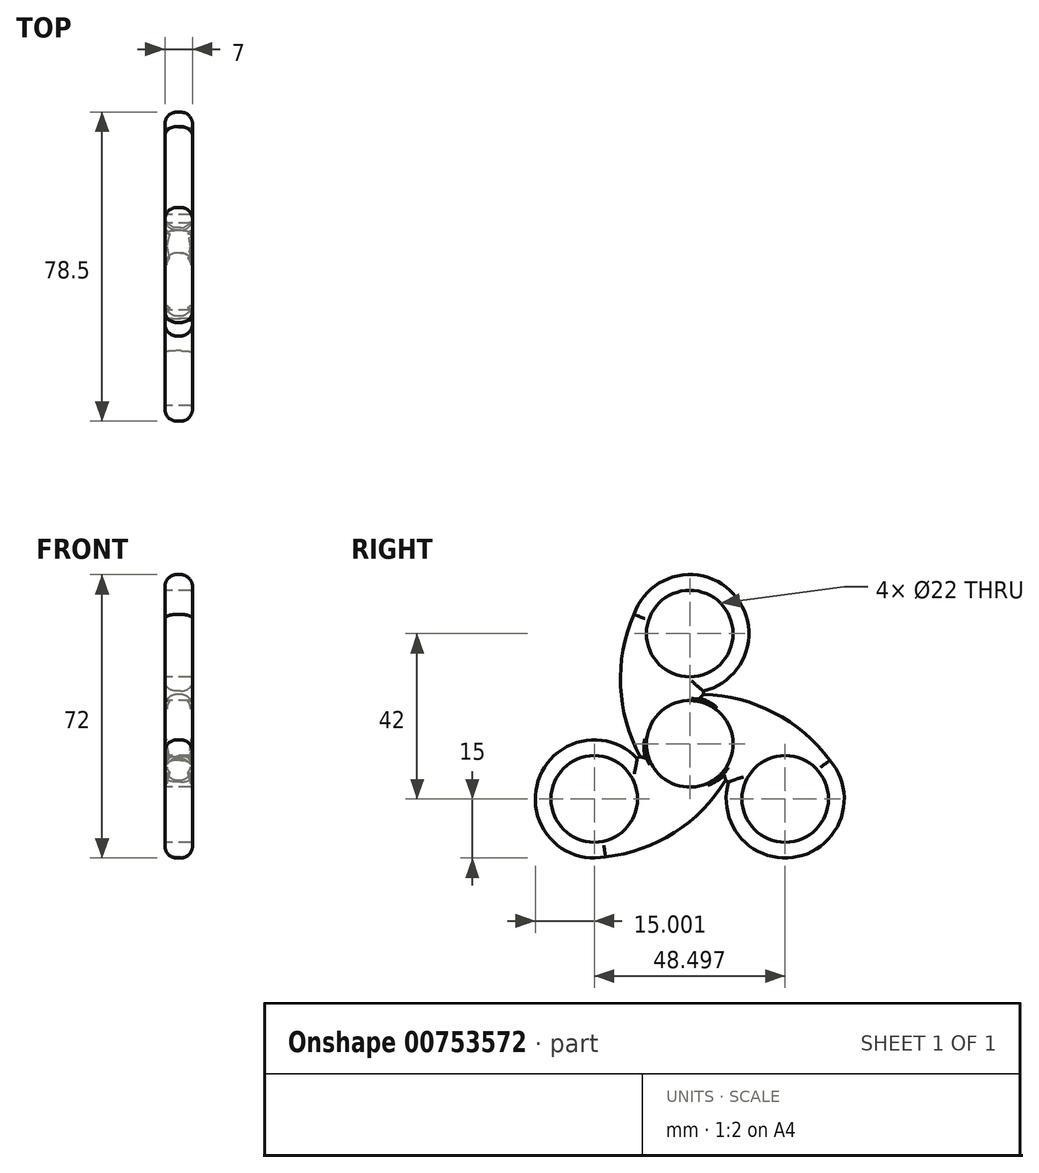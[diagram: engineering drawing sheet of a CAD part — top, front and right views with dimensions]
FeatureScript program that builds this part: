
annotation { "Feature Type Name" : "Feature", "Feature Type Description" : "" }
export const myFeature = defineFeature(function(context is Context, id is Id, definition is map)
    precondition{}
    {
        {
            var Q0;
            Q0=qCreatedBy(makeId("Right.planeOp"),FACE);
            var sketch = newSketch(context, id + "F0", { "sketchPlane" : qUnion([Q0])});
            skCircle(sketch, "E0", {"center": v(0, 0) * mm, "radius": 13 * mm});
            skCircle(sketch, "E1", {"center": v(0, 0) * mm, "radius": 11 * mm});
            skPoint(sketch, "E2", {"position": v(0, 28) * mm});
            skCircle(sketch, "E3", {"center": v(0, 28) * mm, "radius": 15 * mm});
            skCircle(sketch, "E4", {"center": v(0, 28) * mm, "radius": 11 * mm});
            skCircle(sketch, "E5.1.0", {"center": v(-24.25, -14) * mm, "radius": 15 * mm});
            skCircle(sketch, "E5.2.0", {"center": v(24.25, -14) * mm, "radius": 15 * mm});
            skCircle(sketch, "E6.1.0", {"center": v(-24.25, -14) * mm, "radius": 11 * mm});
            skCircle(sketch, "E6.2.0", {"center": v(24.25, -14) * mm, "radius": 11 * mm});
            skArc(sketch, "E7", {"start": v(-12.54, 36.23) * mm, "mid": v(-17.6, 16.5) * mm, "end": v(-12.58, -3.26) * mm});
            skArc(sketch, "E8.1.1", {"start": v(-25.1, -28.98) * mm, "mid": v(-5.48, -23.5) * mm, "end": v(9.12, -9.27) * mm});
            skArc(sketch, "E8.2.1", {"start": v(37.65, -7.26) * mm, "mid": v(23.09, 7) * mm, "end": v(3.47, 12.53) * mm});
            skArc(sketch, "E9", {"start": v(-12, 19) * mm, "mid": v(-12.12, 13.22) * mm, "end": v(-10.51, 7.65) * mm});
            skArc(sketch, "E10.1.0", {"start": v(-10.46, -19.9) * mm, "mid": v(-5.38, -17.1) * mm, "end": v(-1.37, -12.93) * mm});
            skArc(sketch, "E10.2.0", {"start": v(22.47, 0.9) * mm, "mid": v(17.5, 3.9) * mm, "end": v(11.88, 5.28) * mm});
            skLineSegment(sketch, "E11", {"start": v(-12.58, -3.26) * mm, "end": v(-13.35, -3.7) * mm});
            skLineSegment(sketch, "E12.1.0", {"start": v(9.12, -9.27) * mm, "end": v(9.88, -9.7) * mm});
            skLineSegment(sketch, "E12.2.0", {"start": v(3.47, 12.53) * mm, "end": v(3.47, 13.4) * mm});
            skLineSegment(sketch, "E13", {"start": v(-4.37, 12.24) * mm, "end": v(-4.37, 13.65) * mm});
            skLineSegment(sketch, "E14.1.0", {"start": v(-8.42, -9.9) * mm, "end": v(-9.64, -10.61) * mm});
            skLineSegment(sketch, "E14.2.0", {"start": v(12.79, -2.34) * mm, "end": v(14, -3.04) * mm});
            skSolve(sketch);
        }
        {
            var Q0;
            Q0 = qSketchRegion(id + "F0", true);
            var Q1;
            {var subQ0=sQuery(id+"F0.wireOp",EDGE,"E13");Q1=makeQuery(id+"F0.imprint","IMPRINT",FACE,{"disambiguationData":[TD([[makeQuery(id+"F0.imprint","IMPRINT",EDGE,{"derivedFrom":subQ0}),-1.0]])]});}
            var Q2;
            {var subQ0=sQuery(id+"F0.wireOp",EDGE,"E14.2.0");Q2=makeQuery(id+"F0.imprint","IMPRINT",FACE,{"disambiguationData":[TD([[makeQuery(id+"F0.imprint","IMPRINT",EDGE,{"derivedFrom":subQ0}),-1.0]])]});}
            var Q3;
            {var subQ0=sQuery(id+"F0.wireOp",EDGE,"E14.1.0");Q3=makeQuery(id+"F0.imprint","IMPRINT",FACE,{"disambiguationData":[TD([[makeQuery(id+"F0.imprint","IMPRINT",EDGE,{"derivedFrom":subQ0}),-1.0]])]});}
            var Q4;
            {var subQ0=sQuery(id+"F0.wireOp",EDGE,"E9");Q4=makeQuery(id+"F0.imprint","IMPRINT",FACE,{"disambiguationData":[TD([[makeQuery(id+"F0.imprint","IMPRINT",EDGE,{"derivedFrom":subQ0}),1.0]])]});}
            var Q5;
            {var subQ0=sQuery(id+"F0.wireOp",EDGE,"E10.2.0");Q5=makeQuery(id+"F0.imprint","IMPRINT",FACE,{"disambiguationData":[TD([[makeQuery(id+"F0.imprint","IMPRINT",EDGE,{"derivedFrom":subQ0}),1.0]])]});}
            var Q6;
            {var subQ0=sQuery(id+"F0.wireOp",EDGE,"E10.1.0");Q6=makeQuery(id+"F0.imprint","IMPRINT",FACE,{"disambiguationData":[TD([[makeQuery(id+"F0.imprint","IMPRINT",EDGE,{"derivedFrom":subQ0}),1.0]])]});}
            extrude(context, id + "F1", {"entities" : qUnion([Q0, Q1, Q2, Q3, Q4, Q5, Q6]), "depth" : 7 * mm, "offsetDistance" : 25.4 * mm});
        }
        {
            var Q0;
            {var subQ0=sQuery(id+"F0.wireOp",EDGE,"E0");Q0=makeQuery(id+"F1.opExtrude","CAP_EDGE",EDGE,{"disambiguationData":[OSD([subQ0]),TDD([makeQuery(id+"F0.imprint","IMPRINT",EDGE,{"disambiguationData":[TD([[makeQuery(id+"F0.imprint","INTERSECT",VERTEX,{"derivedFrom":[subQ0,sQuery(id+"F0.wireOp",EDGE,"E10.1.0")]}),1.0]])],"derivedFrom":subQ0})])],"isStart":true});}
            var Q1;
            Q1=makeQuery(id+"F1.opExtrude","CAP_EDGE",EDGE,{"disambiguationData":[OSD([sQuery(id+"F0.wireOp",EDGE,"E14.1.0")])],"isStart":true});
            var Q2;
            {var subQ0=sQuery(id+"F0.wireOp",EDGE,"E5.1.0");Q2=makeQuery(id+"F1.opExtrude","CAP_EDGE",EDGE,{"disambiguationData":[OSD([subQ0]),TDD([makeQuery(id+"F0.imprint","IMPRINT",EDGE,{"disambiguationData":[TD([[makeQuery(id+"F0.imprint","INTERSECT",VERTEX,{"derivedFrom":[subQ0,sQuery(id+"F0.wireOp",EDGE,"E10.1.0")]}),-1.0]])],"derivedFrom":subQ0})])],"isStart":true});}
            var Q3;
            Q3=makeQuery(id+"F1.opExtrude","CAP_EDGE",EDGE,{"disambiguationData":[OSD([sQuery(id+"F0.wireOp",EDGE,"E10.1.0")])],"isStart":true});
            var Q4;
            Q4=makeQuery(id+"F1.opExtrude","CAP_EDGE",EDGE,{"disambiguationData":[OSD([sQuery(id+"F0.wireOp",EDGE,"E10.2.0")])],"isStart":true});
            var Q5;
            {var subQ0=sQuery(id+"F0.wireOp",EDGE,"E5.2.0");Q5=makeQuery(id+"F1.opExtrude","CAP_EDGE",EDGE,{"disambiguationData":[OSD([subQ0]),TDD([makeQuery(id+"F0.imprint","IMPRINT",EDGE,{"disambiguationData":[TD([[makeQuery(id+"F0.imprint","INTERSECT",VERTEX,{"derivedFrom":[subQ0,sQuery(id+"F0.wireOp",EDGE,"E10.2.0")]}),-1.0]])],"derivedFrom":subQ0})])],"isStart":true});}
            var Q6;
            Q6=makeQuery(id+"F1.opExtrude","CAP_EDGE",EDGE,{"disambiguationData":[OSD([sQuery(id+"F0.wireOp",EDGE,"E14.2.0")])],"isStart":true});
            var Q7;
            {var subQ0=sQuery(id+"F0.wireOp",EDGE,"E0");Q7=makeQuery(id+"F1.opExtrude","CAP_EDGE",EDGE,{"disambiguationData":[OSD([subQ0]),TDD([makeQuery(id+"F0.imprint","IMPRINT",EDGE,{"disambiguationData":[TD([[makeQuery(id+"F0.imprint","INTERSECT",VERTEX,{"derivedFrom":[subQ0,sQuery(id+"F0.wireOp",EDGE,"E10.2.0")]}),1.0]])],"derivedFrom":subQ0})])],"isStart":true});}
            var Q8;
            Q8=makeQuery(id+"F1.opExtrude","CAP_EDGE",EDGE,{"disambiguationData":[OSD([sQuery(id+"F0.wireOp",EDGE,"E13")])],"isStart":true});
            var Q9;
            {var subQ0=sQuery(id+"F0.wireOp",EDGE,"E0");Q9=makeQuery(id+"F1.opExtrude","CAP_EDGE",EDGE,{"disambiguationData":[OSD([subQ0]),TDD([makeQuery(id+"F0.imprint","IMPRINT",EDGE,{"disambiguationData":[TD([[makeQuery(id+"F0.imprint","INTERSECT",VERTEX,{"derivedFrom":[subQ0,sQuery(id+"F0.wireOp",EDGE,"E9")]}),1.0]])],"derivedFrom":subQ0})])],"isStart":true});}
            var Q10;
            Q10=makeQuery(id+"F1.opExtrude","CAP_EDGE",EDGE,{"disambiguationData":[OSD([sQuery(id+"F0.wireOp",EDGE,"E9")])],"isStart":true});
            var Q11;
            {var subQ0=sQuery(id+"F0.wireOp",EDGE,"E3");Q11=makeQuery(id+"F1.opExtrude","CAP_EDGE",EDGE,{"disambiguationData":[OSD([subQ0]),TDD([makeQuery(id+"F0.imprint","IMPRINT",EDGE,{"disambiguationData":[TD([[makeQuery(id+"F0.imprint","INTERSECT",VERTEX,{"derivedFrom":[subQ0,sQuery(id+"F0.wireOp",EDGE,"E9")]}),-1.0]])],"derivedFrom":subQ0})])],"isStart":true});}
            var Q12;
            {var subQ0=sQuery(id+"F0.wireOp",EDGE,"E0");Q12=makeQuery(id+"F1.opExtrude","CAP_EDGE",EDGE,{"disambiguationData":[OSD([subQ0]),TDD([makeQuery(id+"F0.imprint","IMPRINT",EDGE,{"disambiguationData":[TD([[makeQuery(id+"F0.imprint","INTERSECT",VERTEX,{"derivedFrom":[subQ0,sQuery(id+"F0.wireOp",EDGE,"E9")]}),1.0]])],"derivedFrom":subQ0})])],"isStart":false});}
            var Q13;
            Q13=makeQuery(id+"F1.opExtrude","CAP_EDGE",EDGE,{"disambiguationData":[OSD([sQuery(id+"F0.wireOp",EDGE,"E9")])],"isStart":false});
            var Q14;
            Q14=makeQuery(id+"F1.opExtrude","CAP_EDGE",EDGE,{"disambiguationData":[OSD([sQuery(id+"F0.wireOp",EDGE,"E13")])],"isStart":false});
            var Q15;
            {var subQ0=sQuery(id+"F0.wireOp",EDGE,"E3");Q15=makeQuery(id+"F1.opExtrude","CAP_EDGE",EDGE,{"disambiguationData":[OSD([subQ0]),TDD([makeQuery(id+"F0.imprint","IMPRINT",EDGE,{"disambiguationData":[TD([[makeQuery(id+"F0.imprint","INTERSECT",VERTEX,{"derivedFrom":[subQ0,sQuery(id+"F0.wireOp",EDGE,"E9")]}),-1.0]])],"derivedFrom":subQ0})])],"isStart":false});}
            var Q16;
            {var subQ0=sQuery(id+"F0.wireOp",EDGE,"E0");Q16=makeQuery(id+"F1.opExtrude","CAP_EDGE",EDGE,{"disambiguationData":[OSD([subQ0]),TDD([makeQuery(id+"F0.imprint","IMPRINT",EDGE,{"disambiguationData":[TD([[makeQuery(id+"F0.imprint","INTERSECT",VERTEX,{"derivedFrom":[subQ0,sQuery(id+"F0.wireOp",EDGE,"E10.2.0")]}),1.0]])],"derivedFrom":subQ0})])],"isStart":false});}
            var Q17;
            Q17=makeQuery(id+"F1.opExtrude","CAP_EDGE",EDGE,{"disambiguationData":[OSD([sQuery(id+"F0.wireOp",EDGE,"E10.2.0")])],"isStart":false});
            var Q18;
            {var subQ0=sQuery(id+"F0.wireOp",EDGE,"E5.2.0");Q18=makeQuery(id+"F1.opExtrude","CAP_EDGE",EDGE,{"disambiguationData":[OSD([subQ0]),TDD([makeQuery(id+"F0.imprint","IMPRINT",EDGE,{"disambiguationData":[TD([[makeQuery(id+"F0.imprint","INTERSECT",VERTEX,{"derivedFrom":[subQ0,sQuery(id+"F0.wireOp",EDGE,"E10.2.0")]}),-1.0]])],"derivedFrom":subQ0})])],"isStart":false});}
            var Q19;
            Q19=makeQuery(id+"F1.opExtrude","CAP_EDGE",EDGE,{"disambiguationData":[OSD([sQuery(id+"F0.wireOp",EDGE,"E14.2.0")])],"isStart":false});
            var Q20;
            {var subQ0=sQuery(id+"F0.wireOp",EDGE,"E7");var subQ1=sQuery(id+"F0.wireOp",EDGE,"E3");var subQ2=makeQuery(id+"F0.imprint","INTERSECT",VERTEX,{"disambiguationData":[OD(0.0)],"derivedFrom":[subQ1,subQ0]});Q20=makeQuery(id+"F1.opExtrude","CAP_EDGE",EDGE,{"disambiguationData":[OSD([subQ1]),TDD([makeQuery(id+"F0.imprint","IMPRINT",EDGE,{"disambiguationData":[TD([[subQ2,-1.0]])],"derivedFrom":subQ1}),makeQuery(id+"F0.imprint","IMPRINT",EDGE,{"disambiguationData":[TD([[subQ2,1.0]])],"derivedFrom":subQ1})])],"isStart":true});}
            var Q21;
            {var subQ0=sQuery(id+"F0.wireOp",EDGE,"E7");var subQ1=sQuery(id+"F0.wireOp",EDGE,"E3");var subQ2=makeQuery(id+"F0.imprint","INTERSECT",VERTEX,{"disambiguationData":[OD(0.0)],"derivedFrom":[subQ1,subQ0]});Q21=makeQuery(id+"F1.opExtrude","CAP_EDGE",EDGE,{"disambiguationData":[OSD([subQ1]),TDD([makeQuery(id+"F0.imprint","IMPRINT",EDGE,{"disambiguationData":[TD([[subQ2,-1.0]])],"derivedFrom":subQ1}),makeQuery(id+"F0.imprint","IMPRINT",EDGE,{"disambiguationData":[TD([[subQ2,1.0]])],"derivedFrom":subQ1})])],"isStart":false});}
            var Q22;
            Q22=makeQuery(id+"F1.opExtrude","CAP_EDGE",EDGE,{"disambiguationData":[OSD([sQuery(id+"F0.wireOp",EDGE,"E8.2.1")])],"isStart":false});
            var Q23;
            Q23=makeQuery(id+"F1.opExtrude","CAP_EDGE",EDGE,{"disambiguationData":[OSD([sQuery(id+"F0.wireOp",EDGE,"E8.2.1")])],"isStart":true});
            var Q24;
            Q24=makeQuery(id+"F1.opExtrude","CAP_EDGE",EDGE,{"disambiguationData":[OSD([sQuery(id+"F0.wireOp",EDGE,"E8.1.1")])],"isStart":true});
            var Q25;
            Q25=makeQuery(id+"F1.opExtrude","CAP_EDGE",EDGE,{"disambiguationData":[OSD([sQuery(id+"F0.wireOp",EDGE,"E8.1.1")])],"isStart":false});
            var Q26;
            {var subQ0=sQuery(id+"F0.wireOp",EDGE,"E8.1.1");var subQ1=sQuery(id+"F0.wireOp",EDGE,"E5.1.0");var subQ2=makeQuery(id+"F0.imprint","INTERSECT",VERTEX,{"disambiguationData":[OD(0.0)],"derivedFrom":[subQ1,subQ0]});Q26=makeQuery(id+"F1.opExtrude","CAP_EDGE",EDGE,{"disambiguationData":[OSD([subQ1]),TDD([makeQuery(id+"F0.imprint","IMPRINT",EDGE,{"disambiguationData":[TD([[subQ2,-1.0]])],"derivedFrom":subQ1}),makeQuery(id+"F0.imprint","IMPRINT",EDGE,{"disambiguationData":[TD([[subQ2,1.0]])],"derivedFrom":subQ1})])],"isStart":true});}
            var Q27;
            {var subQ0=sQuery(id+"F0.wireOp",EDGE,"E8.1.1");var subQ1=sQuery(id+"F0.wireOp",EDGE,"E5.1.0");var subQ2=makeQuery(id+"F0.imprint","INTERSECT",VERTEX,{"disambiguationData":[OD(0.0)],"derivedFrom":[subQ1,subQ0]});Q27=makeQuery(id+"F1.opExtrude","CAP_EDGE",EDGE,{"disambiguationData":[OSD([subQ1]),TDD([makeQuery(id+"F0.imprint","IMPRINT",EDGE,{"disambiguationData":[TD([[subQ2,-1.0]])],"derivedFrom":subQ1}),makeQuery(id+"F0.imprint","IMPRINT",EDGE,{"disambiguationData":[TD([[subQ2,1.0]])],"derivedFrom":subQ1})])],"isStart":false});}
            var Q28;
            Q28=makeQuery(id+"F1.opExtrude","CAP_EDGE",EDGE,{"disambiguationData":[OSD([sQuery(id+"F0.wireOp",EDGE,"E7")])],"isStart":false});
            var Q29;
            Q29=makeQuery(id+"F1.opExtrude","CAP_EDGE",EDGE,{"disambiguationData":[OSD([sQuery(id+"F0.wireOp",EDGE,"E7")])],"isStart":true});
            var Q30;
            {var subQ0=sQuery(id+"F0.wireOp",EDGE,"E8.2.1");var subQ1=sQuery(id+"F0.wireOp",EDGE,"E5.2.0");var subQ2=makeQuery(id+"F0.imprint","INTERSECT",VERTEX,{"disambiguationData":[OD(0.0)],"derivedFrom":[subQ1,subQ0]});Q30=makeQuery(id+"F1.opExtrude","CAP_EDGE",EDGE,{"disambiguationData":[OSD([subQ1]),TDD([makeQuery(id+"F0.imprint","IMPRINT",EDGE,{"disambiguationData":[TD([[subQ2,-1.0]])],"derivedFrom":subQ1}),makeQuery(id+"F0.imprint","IMPRINT",EDGE,{"disambiguationData":[TD([[subQ2,1.0]])],"derivedFrom":subQ1})])],"isStart":false});}
            var Q31;
            {var subQ0=sQuery(id+"F0.wireOp",EDGE,"E8.2.1");var subQ1=sQuery(id+"F0.wireOp",EDGE,"E5.2.0");var subQ2=makeQuery(id+"F0.imprint","INTERSECT",VERTEX,{"disambiguationData":[OD(0.0)],"derivedFrom":[subQ1,subQ0]});Q31=makeQuery(id+"F1.opExtrude","CAP_EDGE",EDGE,{"disambiguationData":[OSD([subQ1]),TDD([makeQuery(id+"F0.imprint","IMPRINT",EDGE,{"disambiguationData":[TD([[subQ2,-1.0]])],"derivedFrom":subQ1}),makeQuery(id+"F0.imprint","IMPRINT",EDGE,{"disambiguationData":[TD([[subQ2,1.0]])],"derivedFrom":subQ1})])],"isStart":true});}
            var Q32;
            Q32=makeQuery(id+"F1.opExtrude","CAP_EDGE",EDGE,{"disambiguationData":[OSD([sQuery(id+"F0.wireOp",EDGE,"E12.2.0")])],"isStart":true});
            var Q33;
            Q33=makeQuery(id+"F1.opExtrude","CAP_EDGE",EDGE,{"disambiguationData":[OSD([sQuery(id+"F0.wireOp",EDGE,"E12.2.0")])],"isStart":false});
            var Q34;
            Q34=makeQuery(id+"F1.opExtrude","CAP_EDGE",EDGE,{"disambiguationData":[OSD([sQuery(id+"F0.wireOp",EDGE,"E11")])],"isStart":false});
            var Q35;
            Q35=makeQuery(id+"F1.opExtrude","CAP_EDGE",EDGE,{"disambiguationData":[OSD([sQuery(id+"F0.wireOp",EDGE,"E11")])],"isStart":true});
            var Q36;
            Q36=makeQuery(id+"F1.opExtrude","CAP_EDGE",EDGE,{"disambiguationData":[OSD([sQuery(id+"F0.wireOp",EDGE,"E12.1.0")])],"isStart":false});
            var Q37;
            Q37=makeQuery(id+"F1.opExtrude","CAP_EDGE",EDGE,{"disambiguationData":[OSD([sQuery(id+"F0.wireOp",EDGE,"E12.1.0")])],"isStart":true});
            fillet(context, id + "F2", {"entities" : qUnion([Q0, Q1, Q2, Q3, Q4, Q5, Q6, Q7, Q8, Q9, Q10, Q11, Q12, Q13, Q14, Q15, Q16, Q17, Q18, Q19, Q20, Q21, Q22, Q23, Q24, Q25, Q26, Q27, Q28, Q29, Q30, Q31, Q32, Q33, Q34, Q35, Q36, Q37]), "radius" : 3 * mm, "tangentPropagation" : true, "allowEdgeOverflow" : false});
        }
        {
            var Q0;
            Q0=makeQuery(id+"F1.opExtrude","CAP_EDGE",EDGE,{"disambiguationData":[OSD([sQuery(id+"F0.wireOp",EDGE,"E1")])],"isStart":false});
            var Q1;
            Q1=makeQuery(id+"F1.opExtrude","CAP_EDGE",EDGE,{"disambiguationData":[OSD([sQuery(id+"F0.wireOp",EDGE,"E1")])],"isStart":false});
            var Q2;
            Q2=makeQuery(id+"F1.opExtrude","CAP_EDGE",EDGE,{"disambiguationData":[OSD([sQuery(id+"F0.wireOp",EDGE,"E1")])],"isStart":true});
            var Q3;
            Q3=makeQuery(id+"F1.opExtrude","CAP_EDGE",EDGE,{"disambiguationData":[OSD([sQuery(id+"F0.wireOp",EDGE,"E1")])],"isStart":true});
            var Q4;
            Q4=makeQuery(id+"F1.opExtrude","CAP_EDGE",EDGE,{"disambiguationData":[OSD([sQuery(id+"F0.wireOp",EDGE,"E1")])],"isStart":true});
            var Q5;
            Q5=makeQuery(id+"F1.opExtrude","CAP_EDGE",EDGE,{"disambiguationData":[OSD([sQuery(id+"F0.wireOp",EDGE,"E4")])],"isStart":false});
            var Q6;
            Q6=makeQuery(id+"F1.opExtrude","CAP_EDGE",EDGE,{"disambiguationData":[OSD([sQuery(id+"F0.wireOp",EDGE,"E4")])],"isStart":true});
            var Q7;
            Q7=makeQuery(id+"F1.opExtrude","SWEPT_FACE",FACE,{"disambiguationData":[OSD([sQuery(id+"F0.wireOp",EDGE,"E6.2.0")])]});
            var Q8;
            Q8=makeQuery(id+"F1.opExtrude","CAP_EDGE",EDGE,{"disambiguationData":[OSD([sQuery(id+"F0.wireOp",EDGE,"E6.2.0")])],"isStart":true});
            var Q9;
            Q9=makeQuery(id+"F1.opExtrude","CAP_EDGE",EDGE,{"disambiguationData":[OSD([sQuery(id+"F0.wireOp",EDGE,"E6.2.0")])],"isStart":false});
            var Q10;
            Q10=makeQuery(id+"F2.opFillet","BLEND_EDGE",EDGE,{"blendedFrom":[makeQuery(id+"F1.opExtrude","CAP_EDGE",EDGE,{"disambiguationData":[OSD([sQuery(id+"F0.wireOp",EDGE,"E8.2.1")])],"isStart":true}),makeQuery(id+"F1.opExtrude","SWEPT_FACE",FACE,{"disambiguationData":[OSD([sQuery(id+"F0.wireOp",EDGE,"E1")])]})],"blendedInto":[makeQuery(id+"F1.opExtrude","SWEPT_FACE",FACE,{"disambiguationData":[OSD([sQuery(id+"F0.wireOp",EDGE,"E1")])]})]});
            var Q11;
            Q11=makeQuery(id+"F2.opFillet","BLEND_EDGE",EDGE,{"blendedFrom":[makeQuery(id+"F1.opExtrude","CAP_EDGE",EDGE,{"disambiguationData":[OSD([sQuery(id+"F0.wireOp",EDGE,"E8.2.1")])],"isStart":false}),makeQuery(id+"F1.opExtrude","SWEPT_FACE",FACE,{"disambiguationData":[OSD([sQuery(id+"F0.wireOp",EDGE,"E1")])]})],"blendedInto":[makeQuery(id+"F1.opExtrude","SWEPT_FACE",FACE,{"disambiguationData":[OSD([sQuery(id+"F0.wireOp",EDGE,"E1")])]})]});
            var Q12;
            Q12=makeQuery(id+"F2.opFillet","BLEND_EDGE",EDGE,{"blendedFrom":[makeQuery(id+"F1.opExtrude","CAP_EDGE",EDGE,{"disambiguationData":[OSD([sQuery(id+"F0.wireOp",EDGE,"E12.2.0")])],"isStart":false}),makeQuery(id+"F1.opExtrude","SWEPT_FACE",FACE,{"disambiguationData":[OSD([sQuery(id+"F0.wireOp",EDGE,"E1")])]})],"blendedInto":[makeQuery(id+"F1.opExtrude","SWEPT_FACE",FACE,{"disambiguationData":[OSD([sQuery(id+"F0.wireOp",EDGE,"E1")])]})]});
            var Q13;
            Q13=makeQuery(id+"F2.opFillet","BLEND_EDGE",EDGE,{"blendedFrom":[makeQuery(id+"F1.opExtrude","CAP_EDGE",EDGE,{"disambiguationData":[OSD([sQuery(id+"F0.wireOp",EDGE,"E12.2.0")])],"isStart":true}),makeQuery(id+"F1.opExtrude","SWEPT_FACE",FACE,{"disambiguationData":[OSD([sQuery(id+"F0.wireOp",EDGE,"E1")])]})],"blendedInto":[makeQuery(id+"F1.opExtrude","SWEPT_FACE",FACE,{"disambiguationData":[OSD([sQuery(id+"F0.wireOp",EDGE,"E1")])]})]});
            var Q14;
            Q14=makeQuery(id+"F2.opFillet","BLEND_EDGE",EDGE,{"blendedFrom":[makeQuery(id+"F1.opExtrude","CAP_EDGE",EDGE,{"disambiguationData":[OSD([sQuery(id+"F0.wireOp",EDGE,"E11")])],"isStart":false}),makeQuery(id+"F1.opExtrude","SWEPT_FACE",FACE,{"disambiguationData":[OSD([sQuery(id+"F0.wireOp",EDGE,"E1")])]})],"blendedInto":[makeQuery(id+"F1.opExtrude","SWEPT_FACE",FACE,{"disambiguationData":[OSD([sQuery(id+"F0.wireOp",EDGE,"E1")])]})]});
            var Q15;
            Q15=makeQuery(id+"F2.opFillet","BLEND_EDGE",EDGE,{"blendedFrom":[makeQuery(id+"F1.opExtrude","CAP_EDGE",EDGE,{"disambiguationData":[OSD([sQuery(id+"F0.wireOp",EDGE,"E7")])],"isStart":false}),makeQuery(id+"F1.opExtrude","SWEPT_FACE",FACE,{"disambiguationData":[OSD([sQuery(id+"F0.wireOp",EDGE,"E1")])]})],"blendedInto":[makeQuery(id+"F1.opExtrude","SWEPT_FACE",FACE,{"disambiguationData":[OSD([sQuery(id+"F0.wireOp",EDGE,"E1")])]})]});
            var Q16;
            Q16=makeQuery(id+"F2.opFillet","BLEND_EDGE",EDGE,{"blendedFrom":[makeQuery(id+"F1.opExtrude","CAP_EDGE",EDGE,{"disambiguationData":[OSD([sQuery(id+"F0.wireOp",EDGE,"E7")])],"isStart":true}),makeQuery(id+"F1.opExtrude","SWEPT_FACE",FACE,{"disambiguationData":[OSD([sQuery(id+"F0.wireOp",EDGE,"E1")])]})],"blendedInto":[makeQuery(id+"F1.opExtrude","SWEPT_FACE",FACE,{"disambiguationData":[OSD([sQuery(id+"F0.wireOp",EDGE,"E1")])]})]});
            var Q17;
            Q17=makeQuery(id+"F2.opFillet","BLEND_EDGE",EDGE,{"blendedFrom":[makeQuery(id+"F1.opExtrude","CAP_EDGE",EDGE,{"disambiguationData":[OSD([sQuery(id+"F0.wireOp",EDGE,"E11")])],"isStart":true}),makeQuery(id+"F1.opExtrude","SWEPT_FACE",FACE,{"disambiguationData":[OSD([sQuery(id+"F0.wireOp",EDGE,"E1")])]})],"blendedInto":[makeQuery(id+"F1.opExtrude","SWEPT_FACE",FACE,{"disambiguationData":[OSD([sQuery(id+"F0.wireOp",EDGE,"E1")])]})]});
            var Q18;
            Q18=makeQuery(id+"F2.opFillet","BLEND_EDGE",EDGE,{"blendedFrom":[makeQuery(id+"F1.opExtrude","CAP_EDGE",EDGE,{"disambiguationData":[OSD([sQuery(id+"F0.wireOp",EDGE,"E8.1.1")])],"isStart":false}),makeQuery(id+"F1.opExtrude","SWEPT_FACE",FACE,{"disambiguationData":[OSD([sQuery(id+"F0.wireOp",EDGE,"E1")])]})],"blendedInto":[makeQuery(id+"F1.opExtrude","SWEPT_FACE",FACE,{"disambiguationData":[OSD([sQuery(id+"F0.wireOp",EDGE,"E1")])]})]});
            var Q19;
            Q19=makeQuery(id+"F2.opFillet","BLEND_EDGE",EDGE,{"blendedFrom":[makeQuery(id+"F1.opExtrude","CAP_EDGE",EDGE,{"disambiguationData":[OSD([sQuery(id+"F0.wireOp",EDGE,"E12.1.0")])],"isStart":false}),makeQuery(id+"F1.opExtrude","SWEPT_FACE",FACE,{"disambiguationData":[OSD([sQuery(id+"F0.wireOp",EDGE,"E1")])]})],"blendedInto":[makeQuery(id+"F1.opExtrude","SWEPT_FACE",FACE,{"disambiguationData":[OSD([sQuery(id+"F0.wireOp",EDGE,"E1")])]})]});
            var Q20;
            Q20=makeQuery(id+"F2.opFillet","BLEND_EDGE",EDGE,{"blendedFrom":[makeQuery(id+"F1.opExtrude","CAP_EDGE",EDGE,{"disambiguationData":[OSD([sQuery(id+"F0.wireOp",EDGE,"E8.1.1")])],"isStart":true}),makeQuery(id+"F1.opExtrude","SWEPT_FACE",FACE,{"disambiguationData":[OSD([sQuery(id+"F0.wireOp",EDGE,"E1")])]})],"blendedInto":[makeQuery(id+"F1.opExtrude","SWEPT_FACE",FACE,{"disambiguationData":[OSD([sQuery(id+"F0.wireOp",EDGE,"E1")])]})]});
            var Q21;
            Q21=makeQuery(id+"F2.opFillet","BLEND_EDGE",EDGE,{"blendedFrom":[makeQuery(id+"F1.opExtrude","CAP_EDGE",EDGE,{"disambiguationData":[OSD([sQuery(id+"F0.wireOp",EDGE,"E12.1.0")])],"isStart":true}),makeQuery(id+"F1.opExtrude","SWEPT_FACE",FACE,{"disambiguationData":[OSD([sQuery(id+"F0.wireOp",EDGE,"E1")])]})],"blendedInto":[makeQuery(id+"F1.opExtrude","SWEPT_FACE",FACE,{"disambiguationData":[OSD([sQuery(id+"F0.wireOp",EDGE,"E1")])]})]});
            var Q22;
            Q22=makeQuery(id+"F1.opExtrude","CAP_EDGE",EDGE,{"disambiguationData":[OSD([sQuery(id+"F0.wireOp",EDGE,"E6.1.0")])],"isStart":false});
            var Q23;
            Q23=makeQuery(id+"F1.opExtrude","CAP_EDGE",EDGE,{"disambiguationData":[OSD([sQuery(id+"F0.wireOp",EDGE,"E6.1.0")])],"isStart":true});
            fillet(context, id + "F3", {"entities" : qUnion([Q0, Q1, Q2, Q3, Q4, Q5, Q6, Q7, Q8, Q9, Q10, Q11, Q12, Q13, Q14, Q15, Q16, Q17, Q18, Q19, Q20, Q21, Q22, Q23]), "radius" : .5 * mm, "tangentPropagation" : true, "allowEdgeOverflow" : false});
        }
    });
